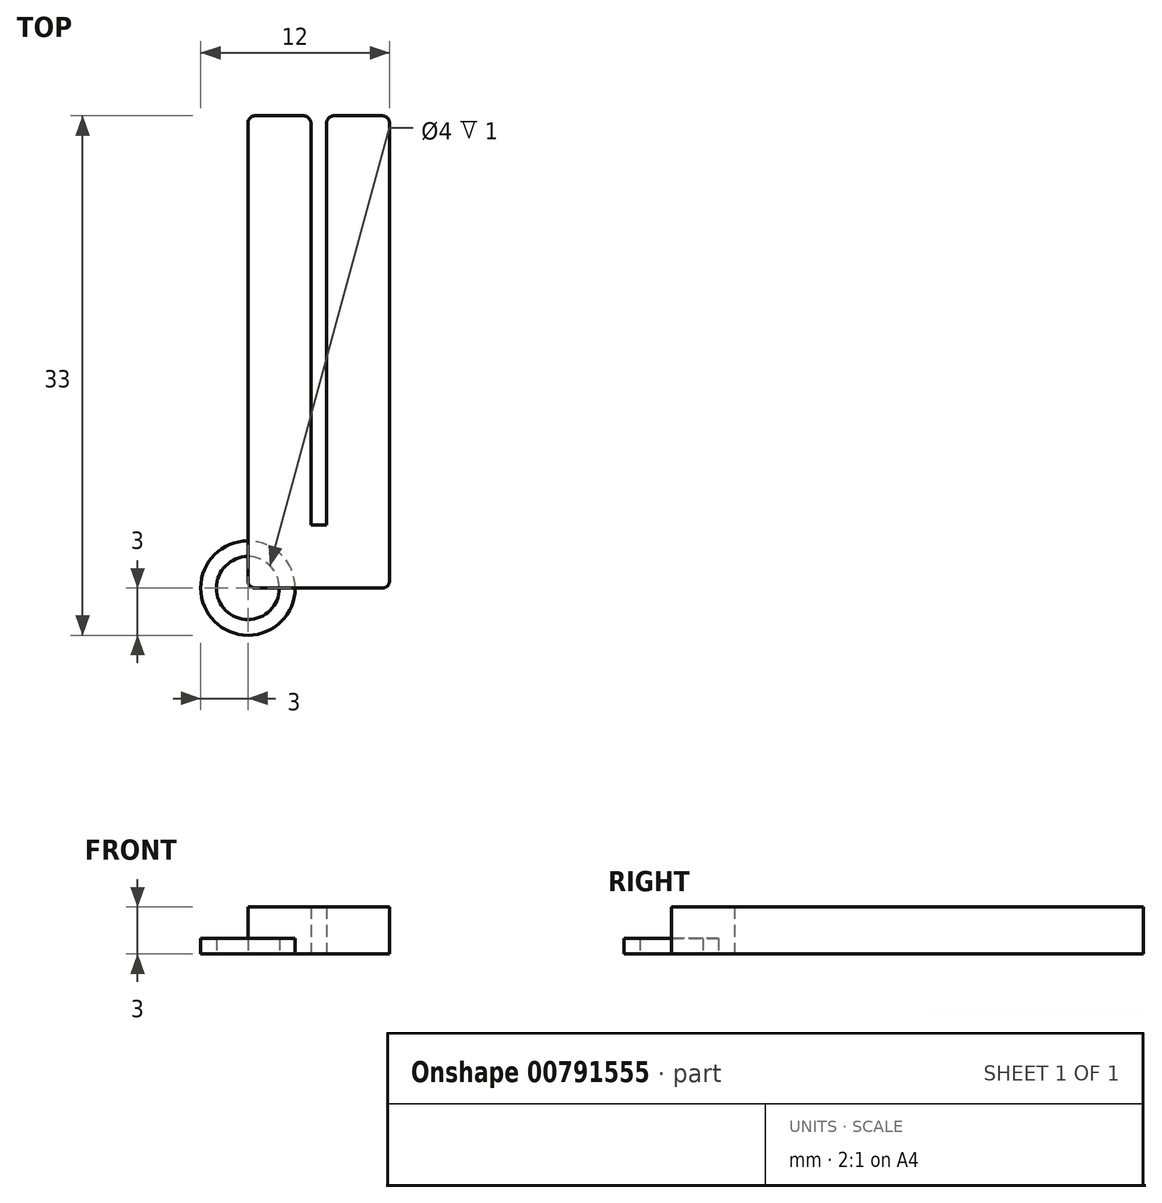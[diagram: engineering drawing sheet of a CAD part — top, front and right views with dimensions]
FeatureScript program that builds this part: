
annotation { "Feature Type Name" : "Feature", "Feature Type Description" : "" }
export const myFeature = defineFeature(function(context is Context, id is Id, definition is map)
    precondition{}
    {
        {
            var Q0;
            Q0=qCreatedBy(makeId("Top.planeOp"),FACE);
            var sketch = newSketch(context, id + "F0", { "sketchPlane" : qUnion([Q0])});
            skLineSegment(sketch, "E0", {"start": v(0, 29.53) * mm, "end": v(0, 0.47) * mm});
            skLineSegment(sketch, "E1", {"start": v(0.47, 0) * mm, "end": v(8.53, 0) * mm});
            skLineSegment(sketch, "E2", {"start": v(9, 0.47) * mm, "end": v(9, 29.53) * mm});
            skLineSegment(sketch, "E3", {"start": v(8.53, 30) * mm, "end": v(5.47, 30) * mm});
            skLineSegment(sketch, "E4", {"start": v(5, 29.53) * mm, "end": v(5, 4) * mm});
            skLineSegment(sketch, "E5", {"start": v(5, 4) * mm, "end": v(4, 4) * mm});
            skLineSegment(sketch, "E6", {"start": v(4, 4) * mm, "end": v(4, 29.53) * mm});
            skLineSegment(sketch, "E7", {"start": v(3.53, 30) * mm, "end": v(0.47, 30) * mm});
            skPoint(sketch, "E8.visualSharp", {"position": v(0, 0) * mm});
            skArc(sketch, "E8.filletArc", {"start": v(0, 0.47) * mm, "mid": v(0.14, 0.14) * mm, "end": v(0.47, 0) * mm});
            skPoint(sketch, "E9.visualSharp", {"position": v(9, 0) * mm});
            skArc(sketch, "E9.filletArc", {"start": v(8.53, 0) * mm, "mid": v(8.86, 0.14) * mm, "end": v(9, 0.47) * mm});
            skPoint(sketch, "E10.visualSharp", {"position": v(4, 30) * mm});
            skArc(sketch, "E10.filletArc", {"start": v(4, 29.53) * mm, "mid": v(3.86, 29.86) * mm, "end": v(3.53, 30) * mm});
            skPoint(sketch, "E11.visualSharp", {"position": v(5, 30) * mm});
            skArc(sketch, "E11.filletArc", {"start": v(5.47, 30) * mm, "mid": v(5.14, 29.86) * mm, "end": v(5, 29.53) * mm});
            skPoint(sketch, "E12.visualSharp", {"position": v(9, 30) * mm});
            skArc(sketch, "E12.filletArc", {"start": v(9, 29.53) * mm, "mid": v(8.86, 29.86) * mm, "end": v(8.53, 30) * mm});
            skPoint(sketch, "E13.visualSharp", {"position": v(0, 30) * mm});
            skArc(sketch, "E13.filletArc", {"start": v(0.47, 30) * mm, "mid": v(0.14, 29.86) * mm, "end": v(0, 29.53) * mm});
            skSolve(sketch);
        }
        {
            var Q0;
            Q0 = qSketchRegion(id + "F0", true);
            extrude(context, id + "F1", {"entities" : qUnion([Q0]), "depth" : 3 * mm, "offsetDistance" : 25 * mm});
        }
        {
            var Q0;
            Q0=qCreatedBy(makeId("Top.planeOp"),FACE);
            var sketch = newSketch(context, id + "F2", { "sketchPlane" : qUnion([Q0])});
            skCircle(sketch, "E14", {"center": v(0, 0) * mm, "radius": 2 * mm});
            skCircle(sketch, "E15", {"center": v(0, 0) * mm, "radius": 3 * mm});
            skSolve(sketch);
        }
        {
            var Q0;
            Q0 = qSketchRegion(id + "F2", true);
            extrude(context, id + "F3", {"entities" : qUnion([Q0]), "depth" : 1 * mm, "offsetDistance" : 25 * mm});
        }
    });
